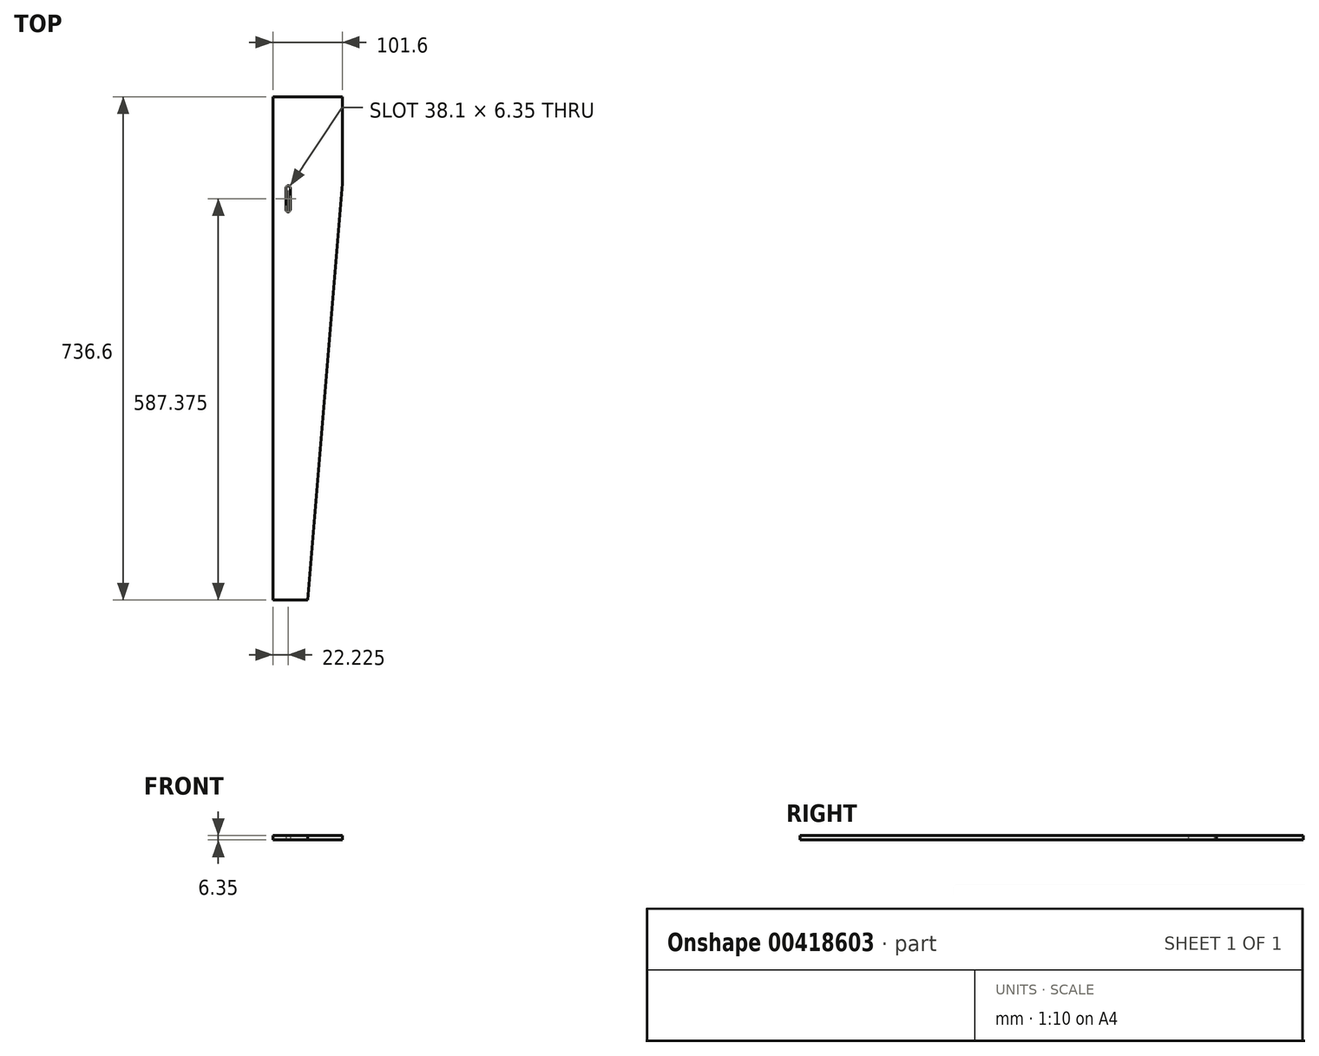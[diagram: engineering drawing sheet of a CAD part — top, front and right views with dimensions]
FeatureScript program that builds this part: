
annotation { "Feature Type Name" : "Feature", "Feature Type Description" : "" }
export const myFeature = defineFeature(function(context is Context, id is Id, definition is map)
    precondition{}
    {
        {
            var Q0;
            Q0=qCreatedBy(makeId("Top.planeOp"),FACE);
            var sketch = newSketch(context, id + "F0", { "sketchPlane" : qUnion([Q0])});
            skLineSegment(sketch, "E0.bottom", {"start": v(0, 0) * mm, "end": v(101.6, 0) * mm});
            skLineSegment(sketch, "E0.top", {"start": v(0, -736.6) * mm, "end": v(50.8, -736.6) * mm});
            skLineSegment(sketch, "E0.right", {"start": v(101.6, 0) * mm, "end": v(101.6, -127) * mm});
            skLineSegment(sketch, "E1", {"start": v(101.6, -127) * mm, "end": v(50.8, -736.6) * mm});
            skLineSegment(sketch, "E2.left", {"start": v(25.4, -133.35) * mm, "end": v(25.4, -165.1) * mm});
            skLineSegment(sketch, "E2.right", {"start": v(19.05, -133.35) * mm, "end": v(19.05, -165.1) * mm});
            skArc(sketch, "E3", {"start": v(19.05, -165.1) * mm, "mid": v(22.23, -168.28) * mm, "end": v(25.4, -165.1) * mm});
            skArc(sketch, "E4", {"start": v(25.4, -133.35) * mm, "mid": v(22.23, -130.17) * mm, "end": v(19.05, -133.35) * mm});
            skPoint(sketch, "E5.center.orphan", {"position": v(22.23, -127) * mm});
            skPoint(sketch, "E6.orphan", {"position": v(25.4, -127) * mm});
            skPoint(sketch, "E7.orphan", {"position": v(19.05, -127) * mm});
            skLineSegment(sketch, "E8.0", {"start": v(0, 0) * mm, "end": v(0, -736.6) * mm});
            skSolve(sketch);
        }
        {
            var Q0;
            Q0 = qSketchRegion(id + "F0", true);
            extrude(context, id + "F1", {"entities" : qUnion([Q0]), "depth" : 6.35 * mm});
        }
    });
